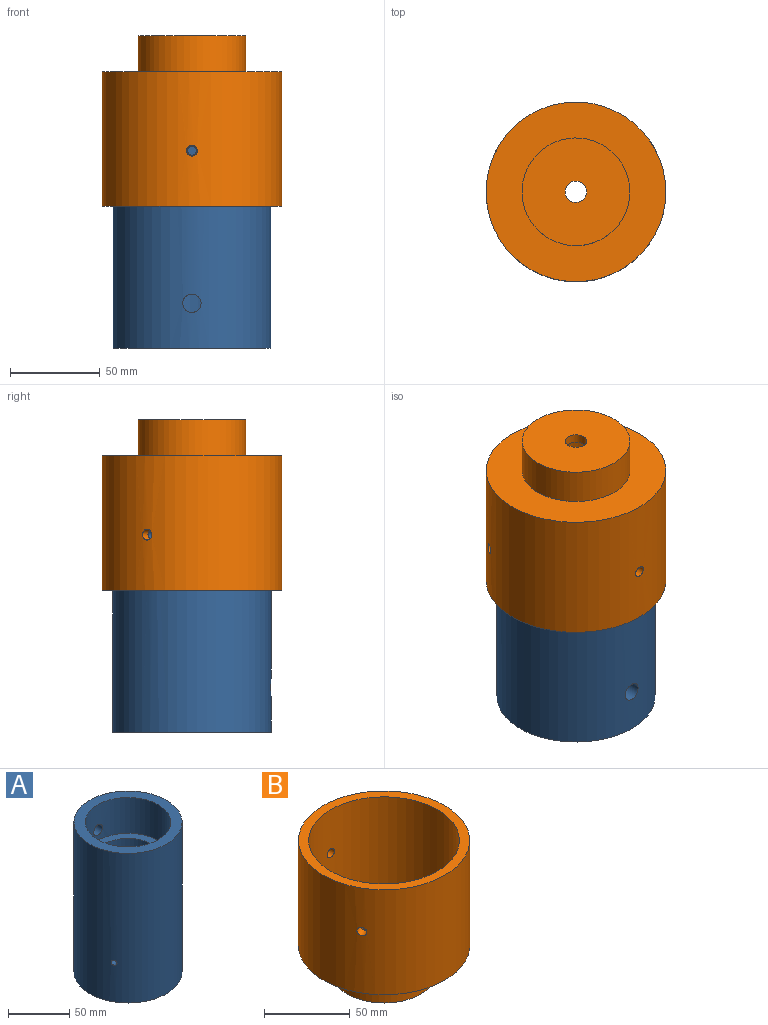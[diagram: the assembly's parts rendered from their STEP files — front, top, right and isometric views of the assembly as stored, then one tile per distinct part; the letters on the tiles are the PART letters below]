
ASSEMBLY  parts=2 mates=1
PART A: 19 faces, bbox 88x88x149 mm
  f0: cylinder r=2.5mm len=10.73mm, axis (-0.87,0.5,0), area 148.7mm2, adj f1,f5
  f1: plane 5x4.33mm, normal (0.87,-0.5,0), area 19.6mm2, adj f0
  f2: cylinder r=2.5mm len=10.73mm, axis (0.87,0.5,0), area 148.7mm2, adj f3,f5
  f3: plane 5x4.33mm, normal (-0.87,-0.5,0), area 19.6mm2, adj f2
  f4: cylinder r=22.5mm len=54.9mm, axis (0,0,1), area 7761.3mm2, adj f10,f14
  f5: cylinder r=44mm len=149mm, axis (0,0,1), area 41051.5mm2, adj f0,f2,f6,f15,f16,f17
  f6: plane 88x88mm, normal (0,0,1), area 2288.5mm2, adj f5,f7
  f7: cylinder r=34.75mm len=69.5mm, axis (0,0,1), area 7690.8mm2, adj f6,f8,f15
  f8: plane 69.5x69.5mm, normal (0,0,1), area 1417.8mm2, adj f7,f9
  f9: cylinder r=27.5mm len=55mm, axis (0,0,1), area 2159.8mm2, adj f8,f10
  f10: plane 55x55mm, normal (0,0,1), area 785.4mm2, adj f4,f9
  f11: cylinder r=31mm len=62mm, axis (0,0,-1), area 6622.5mm2, adj f12,f16
  f12: plane 62x62mm, normal (0,0,-1), area 895.4mm2, adj f11,f13
  f13: cylinder r=26mm len=52mm, axis (0,0,-1), area 1960.4mm2, adj f12,f14
  f14: plane 52x52mm, normal (0,0,-1), area 533.3mm2, adj f4,f13
  f15: cylinder r=5.1mm len=10.2mm, axis (0,-1,0), area 297.7mm2, adj f5,f7
  f16: plane 88x88mm, normal (0,0,-1), area 3063.1mm2, adj f5,f11
  f17: cylinder r=2.5mm len=9.5mm, axis (0,-1,0), area 148.7mm2, adj f5,f18
  f18: plane 5x5mm, normal (0,1,0), area 19.6mm2, adj f17
PART B: 13 faces, bbox 100x100x95 mm
  f0: cylinder r=3mm len=8.29mm, axis (-0.87,0.5,0), area 113.2mm2, adj f2,f3
  f1: cylinder r=3mm len=8.29mm, axis (0.87,0.5,0), area 113.2mm2, adj f2,f3
  f2: cylinder r=44mm len=88mm, axis (0,0,1), area 19267.1mm2, adj f0,f1,f5,f6,f11
  f3: cylinder r=50mm len=100mm, axis (0,0,1), area 23476.9mm2, adj f0,f1,f4,f5,f11
  f4: plane 100x100mm, normal (0,0,-1), area 5026.5mm2, adj f3,f7
  f5: plane 100x100mm, normal (0,0,1), area 1771.9mm2, adj f2,f3
  f6: plane 88x88mm, normal (0,0,1), area 4118.6mm2, adj f2,f8
  f7: cylinder r=30mm len=60mm, axis (0,0,1), area 3769.9mm2, adj f4,f9
  f8: cylinder r=25mm len=50mm, axis (0,0,1), area 3141.6mm2, adj f6,f10
  f9: plane 60x60mm, normal (0,0,-1), area 2714.3mm2, adj f7,f12
  f10: plane 50x50mm, normal (0,0,1), area 1850.4mm2, adj f8,f12
  f11: cylinder r=3mm len=6.1mm, axis (0,-1,0), area 113.2mm2, adj f2,f3
  f12: cylinder r=6mm len=12mm, axis (0,0,1), area 188.5mm2, adj f9,f10
PLACE A rot(axis=(1,0,0),180deg) t=(-88.15,51.92,-207.35)mm
PLACE B rot(axis=(1,0,0),180deg) t=(-88.15,51.92,-78.35)mm
MATE fastened A.f5 <-> B.f3  axis (0,0,1) through (-88.15,51.92,-58.35)mm
